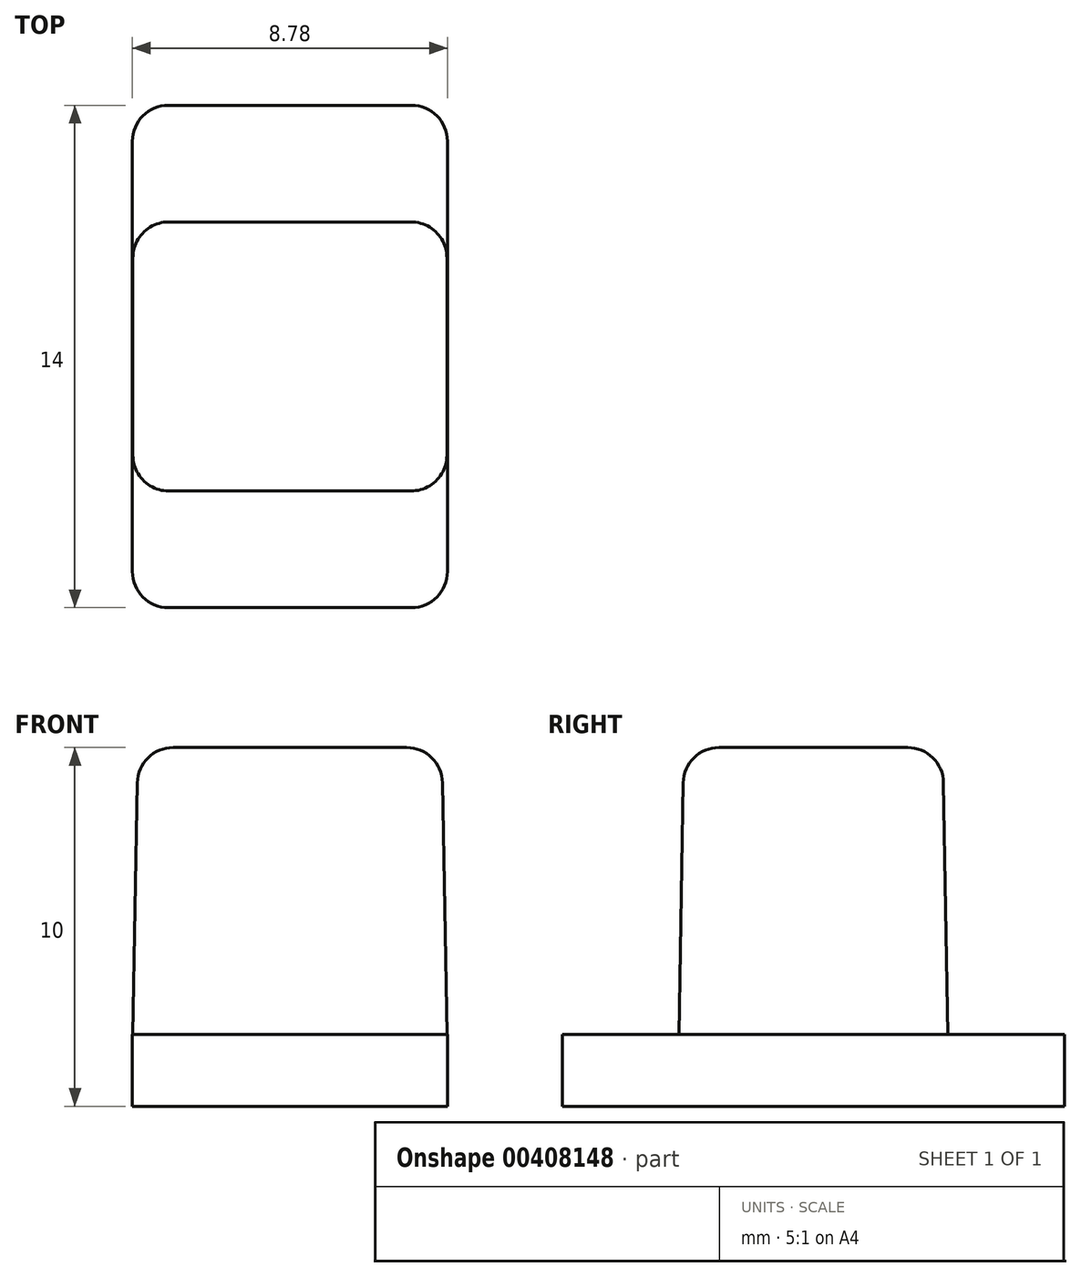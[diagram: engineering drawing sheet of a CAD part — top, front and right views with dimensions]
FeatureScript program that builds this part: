
annotation { "Feature Type Name" : "Feature", "Feature Type Description" : "" }
export const myFeature = defineFeature(function(context is Context, id is Id, definition is map)
    precondition{}
    {
        {
            var Q0;
            Q0=qCreatedBy(makeId("Top.planeOp"),FACE);
            var sketch = newSketch(context, id + "F0", { "sketchPlane" : qUnion([Q0])});
            skLineSegment(sketch, "E0.bottom", {"start": v(4.38, -3.75) * mm, "end": v(-4.38, -3.75) * mm});
            skLineSegment(sketch, "E0.top", {"start": v(4.38, 3.75) * mm, "end": v(-4.38, 3.75) * mm});
            skLineSegment(sketch, "E0.left", {"start": v(4.38, -3.75) * mm, "end": v(4.38, 3.75) * mm});
            skLineSegment(sketch, "E0.right", {"start": v(-4.38, -3.75) * mm, "end": v(-4.38, 3.75) * mm});
            skPoint(sketch, "E0.middle", {"position": v(0, 0) * mm});
            skSolve(sketch);
        }
        {
            var Q0;
            Q0 = qSketchRegion(id + "F0", true);
            extrude(context, id + "F1", {"entities" : qUnion([Q0]), "depth" : 8 * mm, "hasDraft" : true, "draftAngle" : 1 * degree, "draftPullDirection" : true});
        }
        {
            var Q0;
            Q0=makeQuery(id+"F1.opExtrude","CAP_FACE",FACE,{"disambiguationData":[OSD([sQuery(id+"F0.wireOp",EDGE,"E0.bottom"),sQuery(id+"F0.wireOp",EDGE,"E0.top"),sQuery(id+"F0.wireOp",EDGE,"E0.left"),sQuery(id+"F0.wireOp",EDGE,"E0.right")])],"isStart":true});
            var sketch = newSketch(context, id + "F2", { "sketchPlane" : qUnion([Q0])});
            skLineSegment(sketch, "E1.bottom", {"start": v(4.39, -7) * mm, "end": v(-4.39, -7) * mm});
            skLineSegment(sketch, "E1.top", {"start": v(4.39, 7) * mm, "end": v(-4.39, 7) * mm});
            skLineSegment(sketch, "E1.left", {"start": v(4.39, -7) * mm, "end": v(4.39, 7) * mm});
            skLineSegment(sketch, "E1.right", {"start": v(-4.39, -7) * mm, "end": v(-4.39, 7) * mm});
            skPoint(sketch, "E1.middle", {"position": v(0, 0) * mm});
            skSolve(sketch);
        }
        {
            var Q0;
            Q0 = qSketchRegion(id + "F2", true);
            extrude(context, id + "F3", {"entities" : qUnion([Q0]), "operationType" : NewBodyOperationType.ADD, "depth" : 2 * mm});
        }
        {
            var Q0;
            Q0=makeQuery(id+"F1.opExtrude","CAP_FACE",FACE,{"disambiguationData":[OSD([sQuery(id+"F0.wireOp",EDGE,"E0.bottom"),sQuery(id+"F0.wireOp",EDGE,"E0.top"),sQuery(id+"F0.wireOp",EDGE,"E0.left"),sQuery(id+"F0.wireOp",EDGE,"E0.right")])],"isStart":false});
            var Q1;
            Q1=makeQuery(id+"F1.opExtrude","SWEPT_EDGE",EDGE,{"disambiguationData":[OSD([sQuery(id+"F0.wireOp",EDGE,"E0.bottom"),sQuery(id+"F0.wireOp",EDGE,"E0.left")])]});
            var Q2;
            Q2=makeQuery(id+"F1.opExtrude","SWEPT_EDGE",EDGE,{"disambiguationData":[OSD([sQuery(id+"F0.wireOp",EDGE,"E0.bottom"),sQuery(id+"F0.wireOp",EDGE,"E0.right")])]});
            var Q3;
            Q3=makeQuery(id+"F1.opExtrude","SWEPT_EDGE",EDGE,{"disambiguationData":[OSD([sQuery(id+"F0.wireOp",EDGE,"E0.top"),sQuery(id+"F0.wireOp",EDGE,"E0.right")])]});
            var Q4;
            Q4=makeQuery(id+"F1.opExtrude","SWEPT_EDGE",EDGE,{"disambiguationData":[OSD([sQuery(id+"F0.wireOp",EDGE,"E0.top"),sQuery(id+"F0.wireOp",EDGE,"E0.left")])]});
            var Q5;
            Q5=makeQuery(id+"F3.opExtrude","SWEPT_EDGE",EDGE,{"disambiguationData":[OSD([sQuery(id+"F2.wireOp",EDGE,"E1.top"),sQuery(id+"F2.wireOp",EDGE,"E1.left")])]});
            var Q6;
            Q6=makeQuery(id+"F3.opExtrude","SWEPT_EDGE",EDGE,{"disambiguationData":[OSD([sQuery(id+"F2.wireOp",EDGE,"E1.top"),sQuery(id+"F2.wireOp",EDGE,"E1.right")])]});
            var Q7;
            Q7=makeQuery(id+"F3.opExtrude","SWEPT_EDGE",EDGE,{"disambiguationData":[OSD([sQuery(id+"F2.wireOp",EDGE,"E1.bottom"),sQuery(id+"F2.wireOp",EDGE,"E1.left")])]});
            var Q8;
            Q8=makeQuery(id+"F3.opExtrude","SWEPT_EDGE",EDGE,{"disambiguationData":[OSD([sQuery(id+"F2.wireOp",EDGE,"E1.bottom"),sQuery(id+"F2.wireOp",EDGE,"E1.right")])]});
            fillet(context, id + "F4", {"entities" : qUnion([Q0, Q1, Q2, Q3, Q4, Q5, Q6, Q7, Q8]), "radius" : 1 * mm, "tangentPropagation" : true, "allowEdgeOverflow" : false});
        }
    });
